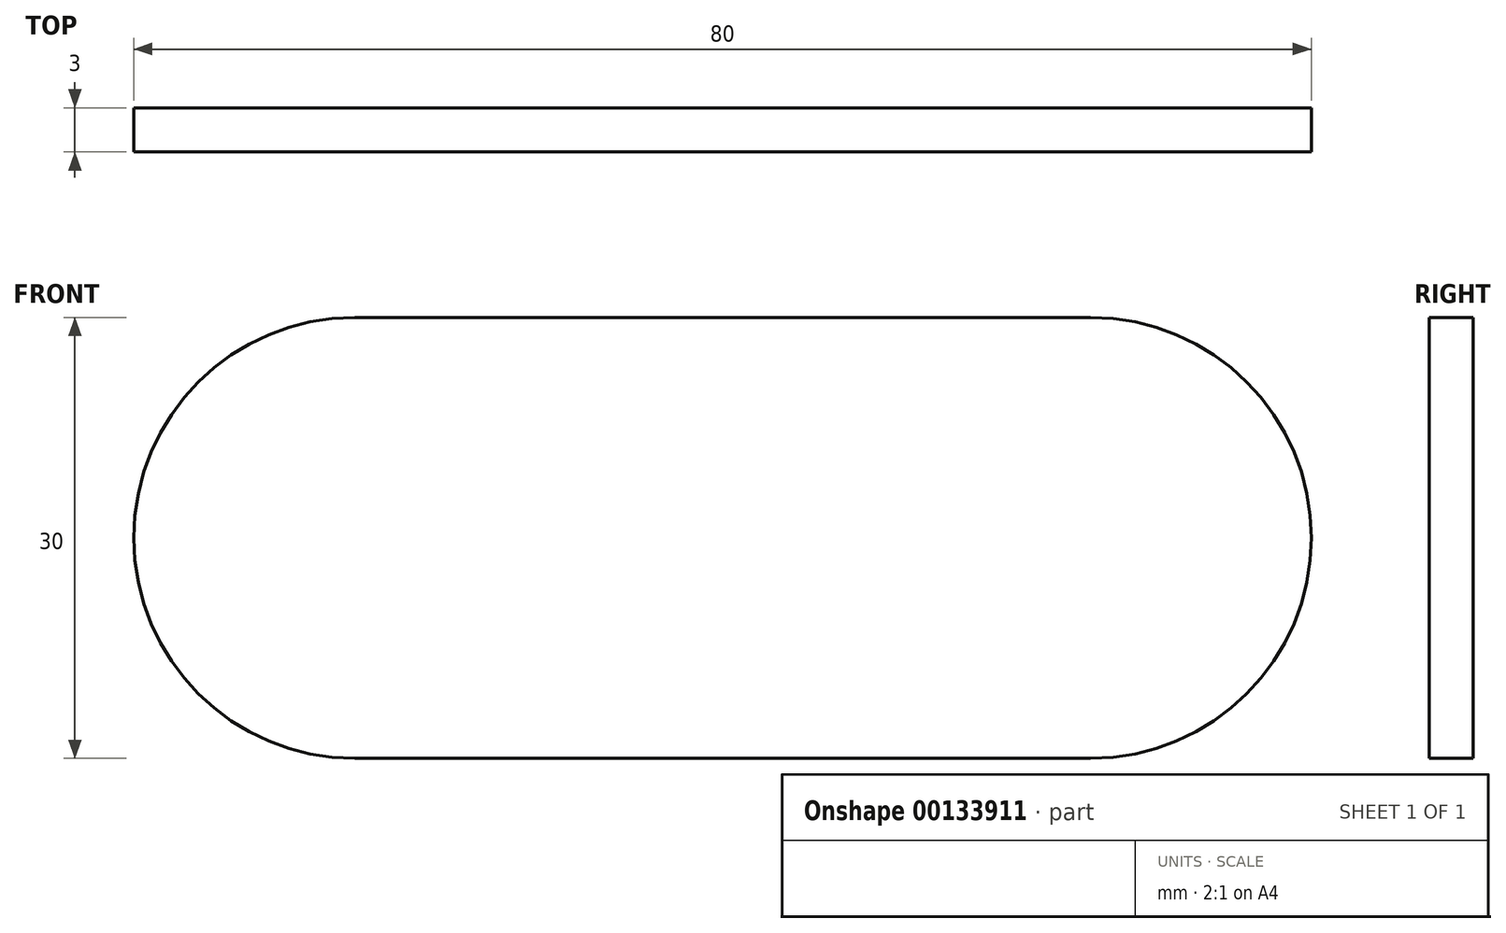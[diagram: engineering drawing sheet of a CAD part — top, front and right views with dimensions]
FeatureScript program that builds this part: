
annotation { "Feature Type Name" : "Feature", "Feature Type Description" : "" }
export const myFeature = defineFeature(function(context is Context, id is Id, definition is map)
    precondition{}
    {
        {
            var Q0;
            Q0=qCreatedBy(makeId("Front.planeOp"),FACE);
            var sketch = newSketch(context, id + "F0", { "sketchPlane" : qUnion([Q0])});
            skLineSegment(sketch, "E0.bottom", {"start": v(0, 0) * mm, "end": v(50, 0) * mm});
            skLineSegment(sketch, "E0.top", {"start": v(0, 30) * mm, "end": v(50, 30) * mm});
            skLineSegment(sketch, "E0.left", {"start": v(0, 0) * mm, "end": v(0, 30) * mm, "construction": true});
            skLineSegment(sketch, "E0.right", {"start": v(50, 0) * mm, "end": v(50, 30) * mm, "construction": true});
            skArc(sketch, "E1", {"start": v(0, 30) * mm, "mid": v(-15, 15) * mm, "end": v(0, 0) * mm});
            skArc(sketch, "E2", {"start": v(50, 0) * mm, "mid": v(65, 15) * mm, "end": v(50, 30) * mm});
            skLineSegment(sketch, "E3", {"start": v(0, 15) * mm, "end": v(-15, 15) * mm, "construction": true});
            skLineSegment(sketch, "E4", {"start": v(50, 15) * mm, "end": v(65, 15) * mm, "construction": true});
            skSolve(sketch);
        }
        {
            var Q0;
            Q0=makeQuery(id+"F0.imprint","IMPRINT",FACE,{"disambiguationData":[TD([[makeQuery(id+"F0.imprint","IMPRINT",EDGE,{"derivedFrom":sQuery(id+"F0.wireOp",EDGE,"E0.bottom")}),1.0]])]});
            extrude(context, id + "F1", {"entities" : qUnion([Q0]), "oppositeDirection" : true, "depth" : 3 * mm});
        }
    });
